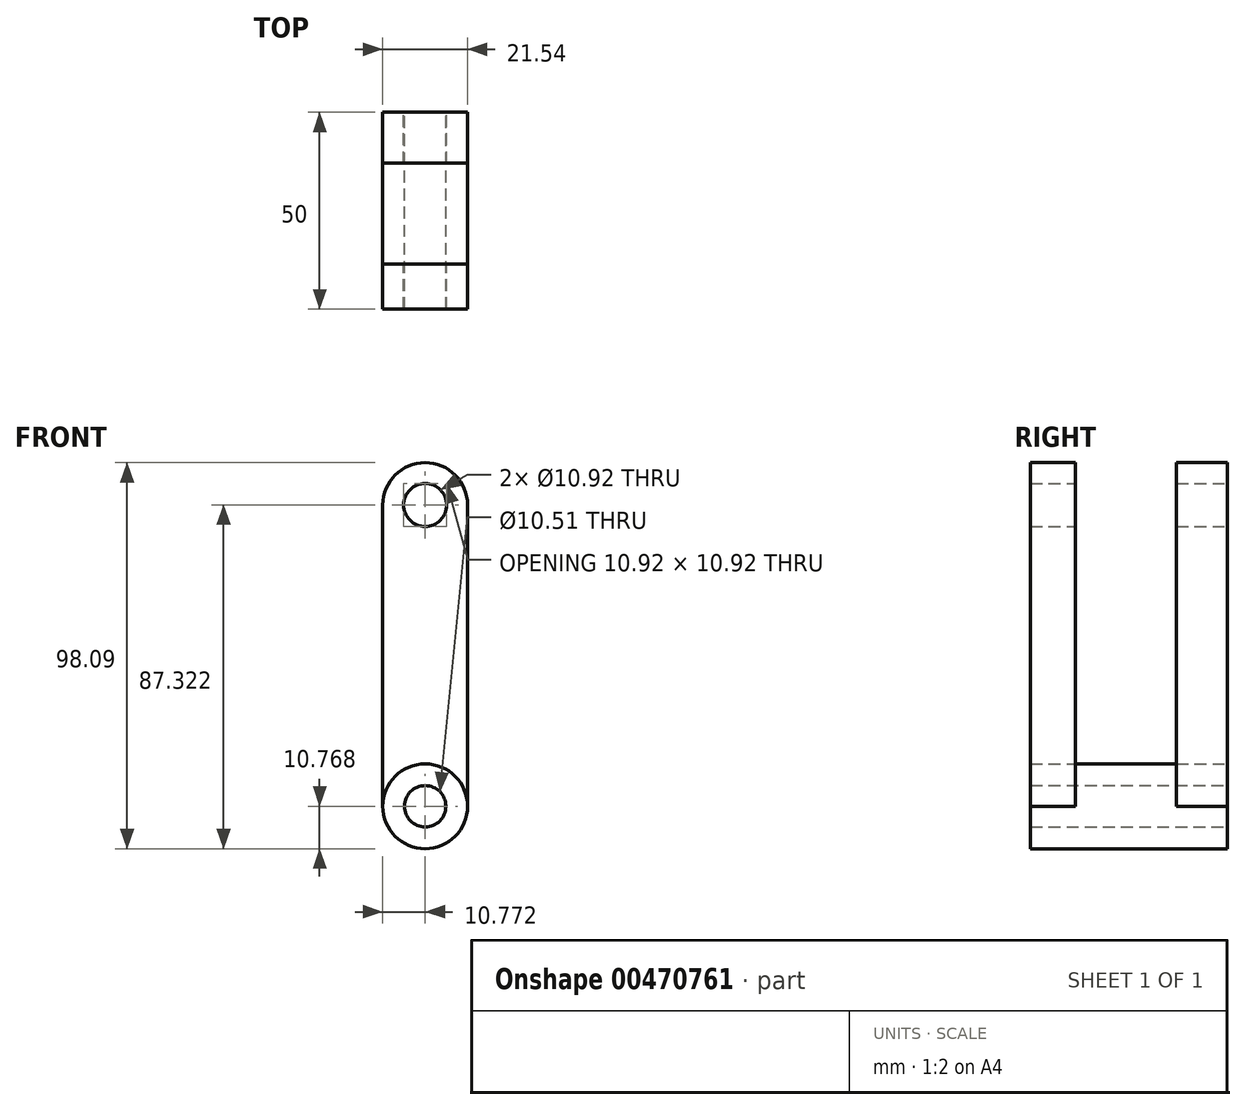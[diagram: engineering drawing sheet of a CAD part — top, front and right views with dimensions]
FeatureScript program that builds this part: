
annotation { "Feature Type Name" : "Feature", "Feature Type Description" : "" }
export const myFeature = defineFeature(function(context is Context, id is Id, definition is map)
    precondition{}
    {
        {
            var Q0;
            Q0=qCreatedBy(makeId("Front.planeOp"),FACE);
            var sketch = newSketch(context, id + "F0", { "sketchPlane" : qUnion([Q0])});
            skLineSegment(sketch, "E0.left", {"start": v(-10.04, -28.34) * mm, "end": v(-10.04, 48.21) * mm});
            skLineSegment(sketch, "E0.right", {"start": v(11.5, -28.34) * mm, "end": v(11.5, 48.21) * mm});
            skCircle(sketch, "E1", {"center": v(0.73, -28.34) * mm, "radius": 10.77 * mm});
            skArc(sketch, "E2", {"start": v(11.5, 48.21) * mm, "mid": v(0.73, 58.98) * mm, "end": v(-10.04, 48.21) * mm});
            skCircle(sketch, "E3", {"center": v(0.73, 48.21) * mm, "radius": 5.46 * mm});
            skCircle(sketch, "E4", {"center": v(0.73, -28.34) * mm, "radius": 5.26 * mm});
            skSolve(sketch);
        }
        {
            var Q0;
            Q0=makeQuery(id+"F0.imprint","IMPRINT",FACE,{"disambiguationData":[TD([[makeQuery(id+"F0.imprint","IMPRINT",EDGE,{"derivedFrom":sQuery(id+"F0.wireOp",EDGE,"E4")}),-1.0]])]});
            extrude(context, id + "F1", {"entities" : qUnion([Q0]), "oppositeDirection" : true, "depth" : 50 * mm});
        }
        {
            var Q0;
            {var subQ1=sQuery(id+"F0.wireOp",EDGE,"E0.left");Q0=makeQuery(id+"F0.imprint","IMPRINT",FACE,{"disambiguationData":[TD([[makeQuery(id+"F0.imprint","IMPRINT",EDGE,{"derivedFrom":subQ1}),-1.0]])]});}
            extrude(context, id + "F2", {"entities" : qUnion([Q0]), "operationType" : NewBodyOperationType.ADD, "oppositeDirection" : true, "depth" : 15 * mm});
        }
        {
            var Q0;
            Q0=makeQuery(id+"F2.opExtrude","CAP_FACE",FACE,{"disambiguationData":[OSD([sQuery(id+"F0.wireOp",EDGE,"E0.left"),sQuery(id+"F0.wireOp",EDGE,"E0.right"),sQuery(id+"F0.wireOp",EDGE,"E1"),sQuery(id+"F0.wireOp",EDGE,"E2"),sQuery(id+"F0.wireOp",EDGE,"E3")])],"isStart":false});
            extrude(context, id + "F3", {"entities" : qUnion([Q0]), "operationType" : NewBodyOperationType.INTERSECT, "depth" : 35 * mm});
        }
        {
            var Q0;
            {var subQ1=sQuery(id+"F0.wireOp",EDGE,"E0.left");Q0=makeQuery(id+"F0.imprint","IMPRINT",FACE,{"disambiguationData":[TD([[makeQuery(id+"F0.imprint","IMPRINT",EDGE,{"derivedFrom":subQ1}),-1.0]])]});}
            extrude(context, id + "F4", {"entities" : qUnion([Q0]), "depth" : 50 * mm});
        }
        {
            var Q0;
            Q0=qCreatedBy(makeId("Right.planeOp"),FACE);
            var sketch = newSketch(context, id + "F5", { "sketchPlane" : qUnion([Q0])});
            skLineSegment(sketch, "E5.bottom", {"start": v(-38.57, 66.82) * mm, "end": v(-12.94, 66.82) * mm});
            skLineSegment(sketch, "E5.top", {"start": v(-38.57, -30.32) * mm, "end": v(-12.94, -30.32) * mm});
            skLineSegment(sketch, "E5.left", {"start": v(-38.57, 66.82) * mm, "end": v(-38.57, -30.32) * mm});
            skLineSegment(sketch, "E5.right", {"start": v(-12.94, 66.82) * mm, "end": v(-12.94, -30.32) * mm});
            skSolve(sketch);
        }
        {
            var Q0;
            Q0=makeQuery(id+"F5.imprint","IMPRINT",FACE,{"disambiguationData":[TD([[makeQuery(id+"F5.imprint","IMPRINT",EDGE,{"derivedFrom":sQuery(id+"F5.wireOp",EDGE,"E5.bottom")}),-1.0]])]});
            extrude(context, id + "F6", {"entities" : qUnion([Q0]), "operationType" : NewBodyOperationType.REMOVE, "depth" : 25 * mm, "hasSecondDirection" : true, "secondDirectionOppositeDirection" : true, "secondDirectionDepth" : 25 * mm});
        }
        {
            var Q0;
            Q0=makeQuery(id+"F0.imprint","IMPRINT",FACE,{"disambiguationData":[TD([[makeQuery(id+"F0.imprint","IMPRINT",EDGE,{"derivedFrom":sQuery(id+"F0.wireOp",EDGE,"E4")}),-1.0]])]});
            extrude(context, id + "F7", {"entities" : qUnion([Q0]), "depth" : 50 * mm});
        }
    });
